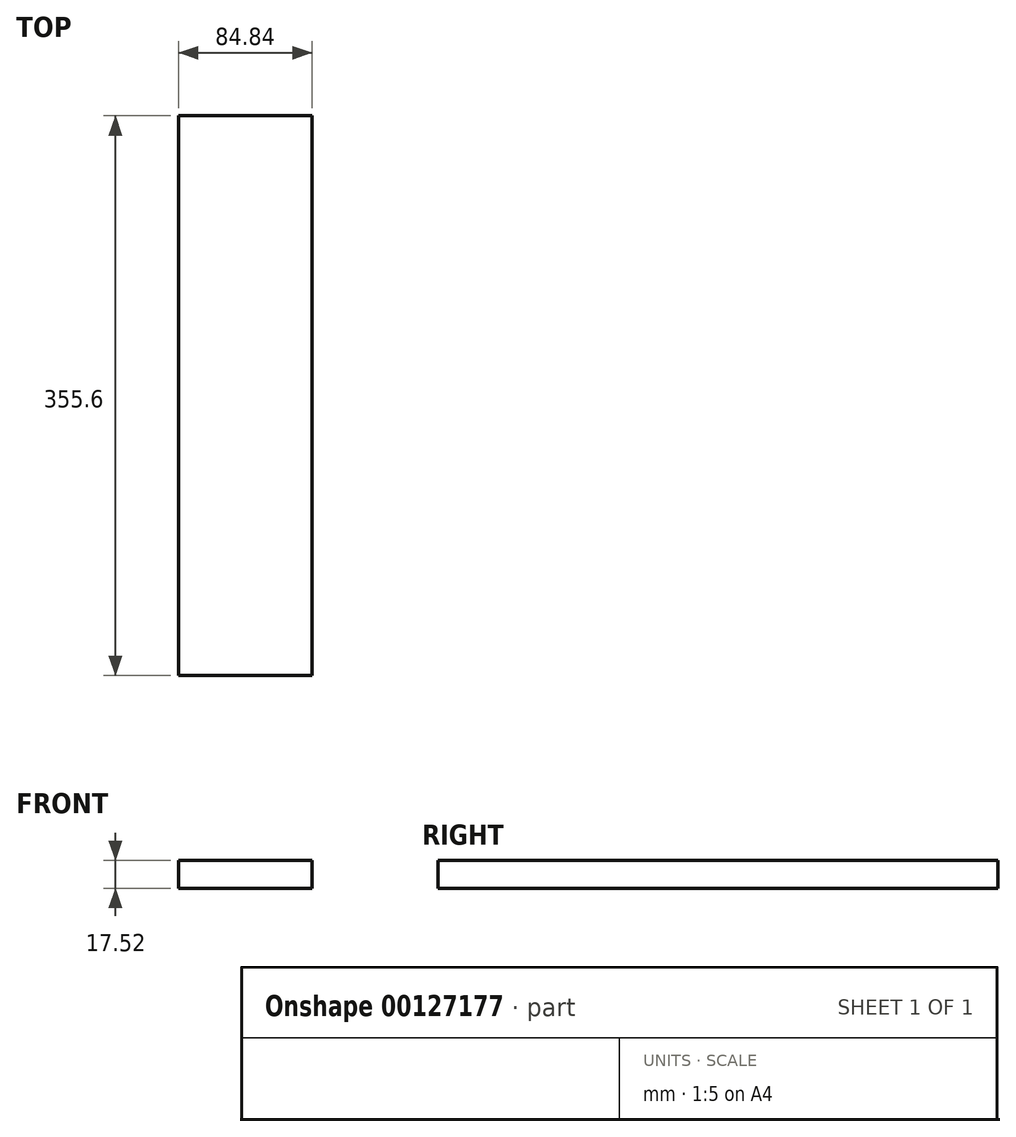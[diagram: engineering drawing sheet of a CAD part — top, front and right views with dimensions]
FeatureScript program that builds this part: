
annotation { "Feature Type Name" : "Feature", "Feature Type Description" : "" }
export const myFeature = defineFeature(function(context is Context, id is Id, definition is map)
    precondition{}
    {
        {
            var Q0;
            Q0=qCreatedBy(makeId("Front.planeOp"),FACE);
            var sketch = newSketch(context, id + "F0", { "sketchPlane" : qUnion([Q0])});
            skLineSegment(sketch, "E0.bottom", {"start": v(42.42, -8.76) * mm, "end": v(-42.42, -8.76) * mm});
            skLineSegment(sketch, "E0.top", {"start": v(42.42, 8.76) * mm, "end": v(-42.42, 8.76) * mm});
            skLineSegment(sketch, "E0.left", {"start": v(42.42, -8.76) * mm, "end": v(42.42, 8.76) * mm});
            skLineSegment(sketch, "E0.right", {"start": v(-42.42, -8.76) * mm, "end": v(-42.42, 8.76) * mm});
            skPoint(sketch, "E0.middle", {"position": v(0, 0) * mm});
            skSolve(sketch);
        }
        {
            var Q0;
            Q0=qSketchRegion(id+"F0",true);
            extrude(context, id + "F1", {"entities" : qUnion([Q0]), "depth" : 355.6 * mm, "offsetDistance" : 25.4 * mm});
        }
    });
